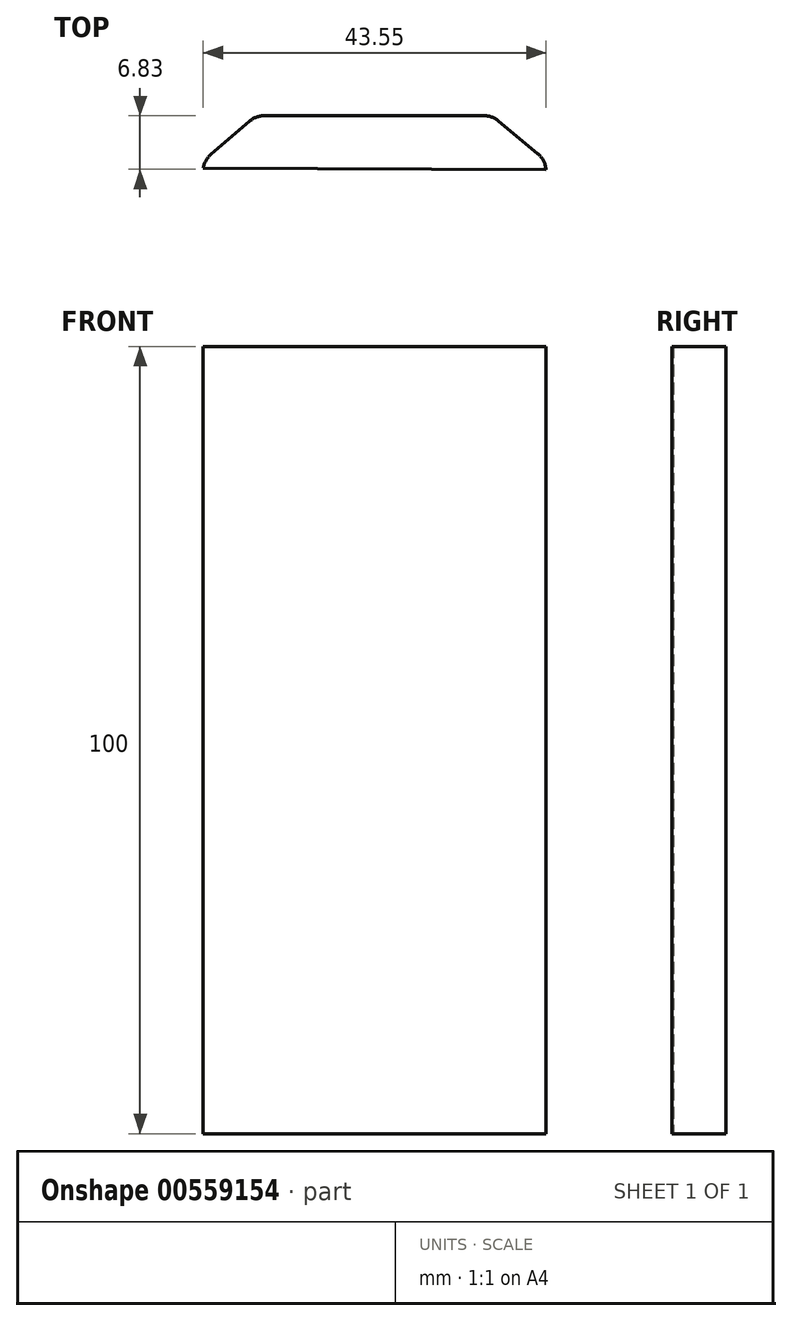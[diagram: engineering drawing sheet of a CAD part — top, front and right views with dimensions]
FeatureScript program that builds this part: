
annotation { "Feature Type Name" : "Feature", "Feature Type Description" : "" }
export const myFeature = defineFeature(function(context is Context, id is Id, definition is map)
    precondition{}
    {
        {
            var Q0;
            Q0=qCreatedBy(makeId("Top.planeOp"),FACE);
            var sketch = newSketch(context, id + "F0", { "sketchPlane" : qUnion([Q0])});
            skLineSegment(sketch, "E0", {"start": v(-38.14, 30) * mm, "end": v(-10.35, 30) * mm});
            skLineSegment(sketch, "E1", {"start": v(-8.42, 29.3) * mm, "end": v(-3.47, 25.17) * mm});
            skLineSegment(sketch, "E2", {"start": v(-2.41, 23.18) * mm, "end": v(-0.11, 1.1) * mm});
            skLineSegment(sketch, "E3", {"start": v(-1.1, 0) * mm, "end": v(-48.81, 0) * mm});
            skLineSegment(sketch, "E4", {"start": v(-49.8, 1.17) * mm, "end": v(-45.96, 23.33) * mm});
            skLineSegment(sketch, "E5", {"start": v(-44.96, 25.1) * mm, "end": v(-40.1, 29.27) * mm});
            skPoint(sketch, "E6.visualSharp", {"position": v(-39.26, 30) * mm});
            skArc(sketch, "E6.filletArc", {"start": v(-38.14, 30) * mm, "mid": v(-39.19, 29.81) * mm, "end": v(-40.1, 29.27) * mm});
            skPoint(sketch, "E7.visualSharp", {"position": v(-45.78, 24.39) * mm});
            skArc(sketch, "E7.filletArc", {"start": v(-44.96, 25.1) * mm, "mid": v(-45.61, 24.3) * mm, "end": v(-45.96, 23.33) * mm});
            skPoint(sketch, "E8.visualSharp", {"position": v(-9.26, 30) * mm});
            skArc(sketch, "E8.filletArc", {"start": v(-8.42, 29.3) * mm, "mid": v(-9.32, 29.82) * mm, "end": v(-10.35, 30) * mm});
            skPoint(sketch, "E9.visualSharp", {"position": v(-2.54, 24.39) * mm});
            skArc(sketch, "E9.filletArc", {"start": v(-2.41, 23.18) * mm, "mid": v(-2.75, 24.28) * mm, "end": v(-3.47, 25.17) * mm});
            skPoint(sketch, "E10.visualSharp", {"position": v(0, 0) * mm});
            skArc(sketch, "E10.filletArc", {"start": v(-1.1, 0) * mm, "mid": v(-0.37, 0.33) * mm, "end": v(-0.11, 1.1) * mm});
            skPoint(sketch, "E11.visualSharp", {"position": v(-50, 0) * mm});
            skArc(sketch, "E11.filletArc", {"start": v(-49.8, 1.17) * mm, "mid": v(-49.58, 0.36) * mm, "end": v(-48.81, 0) * mm});
            skSolve(sketch);
        }
        {
            var Q0;
            Q0=qCreatedBy(makeId("Top.planeOp"),FACE);
            var sketch = newSketch(context, id + "F1", { "sketchPlane" : qUnion([Q0])});
            skLineSegment(sketch, "E12", {"start": v(-3.47, 25.17) * mm, "end": v(-8.42, 29.3) * mm});
            skLineSegment(sketch, "E13", {"start": v(-10.35, 30) * mm, "end": v(-38.14, 30) * mm});
            skPoint(sketch, "E14.visualSharp", {"position": v(-39.26, 30) * mm});
            skArc(sketch, "E14.filletArc", {"start": v(-38.14, 30) * mm, "mid": v(-39.19, 29.81) * mm, "end": v(-40.1, 29.27) * mm});
            skPoint(sketch, "E15.visualSharp", {"position": v(-9.26, 30) * mm});
            skArc(sketch, "E15.filletArc", {"start": v(-8.42, 29.3) * mm, "mid": v(-9.32, 29.82) * mm, "end": v(-10.35, 30) * mm});
            skArc(sketch, "E16", {"start": v(-2.41, 23.17) * mm, "mid": v(-2.75, 24.27) * mm, "end": v(-3.47, 25.17) * mm});
            skLineSegment(sketch, "E17", {"start": v(-40.1, 29.27) * mm, "end": v(-44.97, 25.08) * mm});
            skArc(sketch, "E18", {"start": v(-44.97, 25.08) * mm, "mid": v(-45.62, 24.3) * mm, "end": v(-45.96, 23.33) * mm});
            skLineSegment(sketch, "E19", {"start": v(-45.96, 23.33) * mm, "end": v(-2.41, 23.17) * mm});
            skSolve(sketch);
        }
        {
            var Q0;
            Q0 = qSketchRegion(id + "F1", true);
            extrude(context, id + "F2", {"entities" : qUnion([Q0]), "depth" : 100 * mm, "offsetDistance" : 25 * mm});
        }
    });
